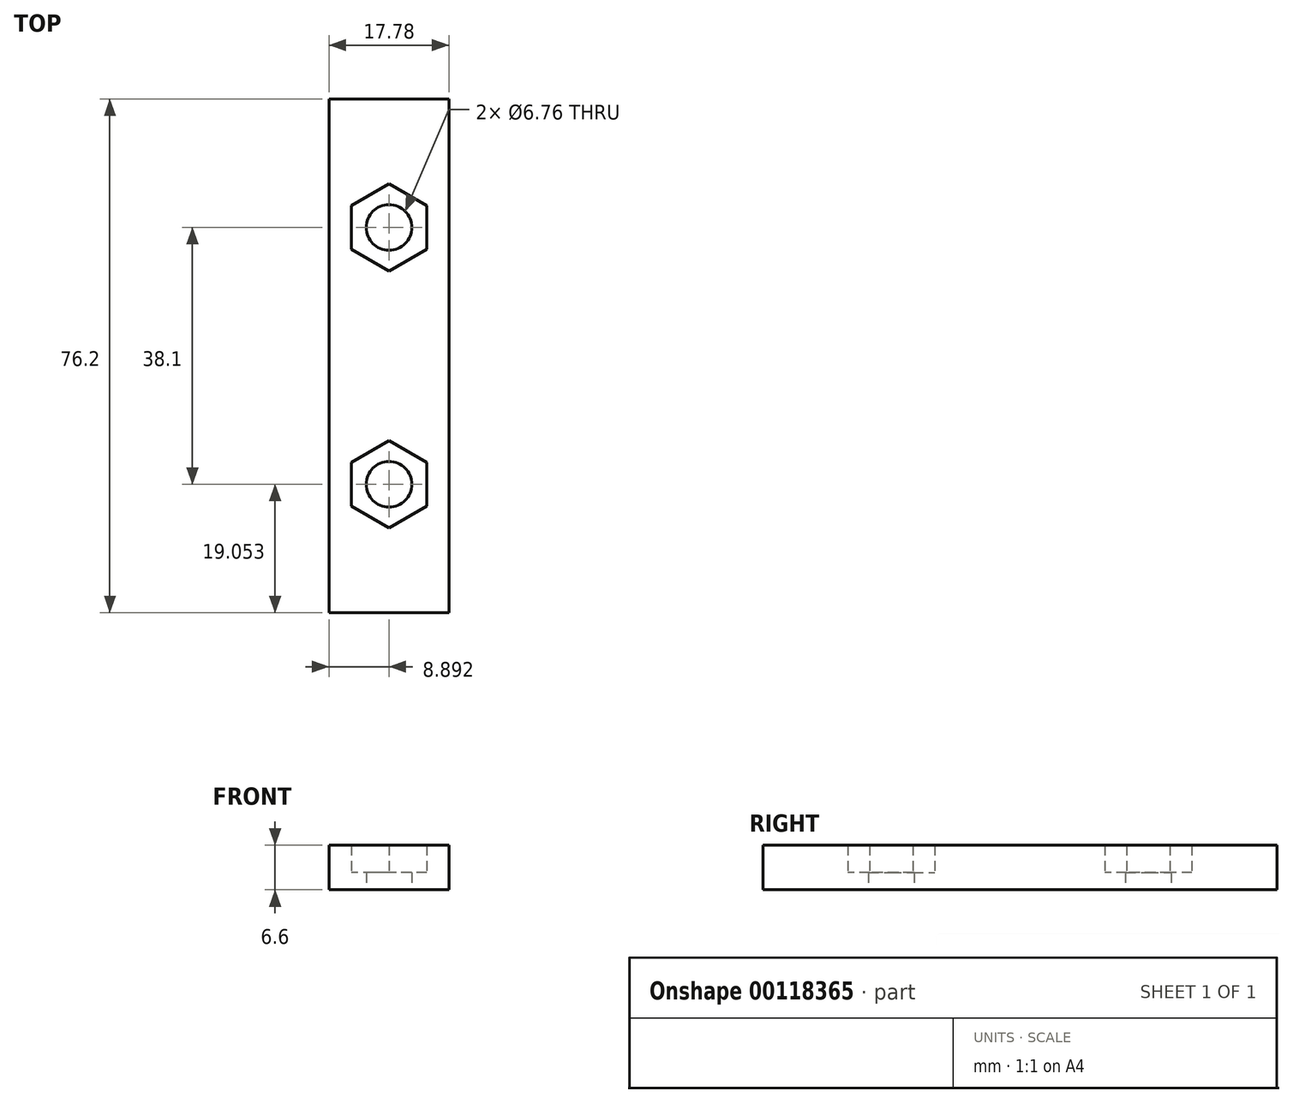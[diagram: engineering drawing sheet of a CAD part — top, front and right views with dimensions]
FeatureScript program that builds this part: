
annotation { "Feature Type Name" : "Feature", "Feature Type Description" : "" }
export const myFeature = defineFeature(function(context is Context, id is Id, definition is map)
    precondition{}
    {
        {
            var Q0;
            Q0=qCreatedBy(makeId("Top.planeOp"),FACE);
            var sketch = newSketch(context, id + "F0", { "sketchPlane" : qUnion([Q0])});
            skLineSegment(sketch, "E0.bottom", {"start": v(-5.89, 167.12) * mm, "end": v(11.9, 167.12) * mm});
            skLineSegment(sketch, "E0.top", {"start": v(-5.89, 90.92) * mm, "end": v(11.9, 90.92) * mm});
            skLineSegment(sketch, "E0.left", {"start": v(-5.89, 167.12) * mm, "end": v(-5.89, 90.92) * mm});
            skLineSegment(sketch, "E0.right", {"start": v(11.9, 167.12) * mm, "end": v(11.9, 90.92) * mm});
            skCircle(sketch, "E1.cCircle", {"center": v(3, 148.07) * mm, "radius": 5.59 * mm, "construction": true});
            skPoint(sketch, "E1.cCircle.centerSnap0", {"position": v(3, 167.12) * mm});
            skLineSegment(sketch, "E1.0", {"start": v(8.59, 151.3) * mm, "end": v(8.59, 144.85) * mm});
            skLineSegment(sketch, "E1.1", {"start": v(8.59, 144.85) * mm, "end": v(3, 141.62) * mm});
            skLineSegment(sketch, "E1.2", {"start": v(3, 141.62) * mm, "end": v(-2.59, 144.85) * mm});
            skLineSegment(sketch, "E1.3", {"start": v(-2.59, 144.85) * mm, "end": v(-2.59, 151.3) * mm});
            skLineSegment(sketch, "E1.4", {"start": v(-2.59, 151.3) * mm, "end": v(3, 154.53) * mm});
            skLineSegment(sketch, "E1.5", {"start": v(3, 154.53) * mm, "end": v(8.59, 151.3) * mm});
            skPoint(sketch, "E1.0.midPoint", {"position": v(8.59, 148.07) * mm});
            skCircle(sketch, "E2.cCircle", {"center": v(3, 109.97) * mm, "radius": 5.59 * mm, "construction": true});
            skLineSegment(sketch, "E2.0", {"start": v(8.59, 106.75) * mm, "end": v(3, 103.52) * mm});
            skLineSegment(sketch, "E2.1", {"start": v(3, 103.52) * mm, "end": v(-2.59, 106.75) * mm});
            skLineSegment(sketch, "E2.2", {"start": v(-2.59, 106.75) * mm, "end": v(-2.59, 113.2) * mm});
            skLineSegment(sketch, "E2.3", {"start": v(-2.59, 113.2) * mm, "end": v(3, 116.43) * mm});
            skLineSegment(sketch, "E2.4", {"start": v(3, 116.43) * mm, "end": v(8.59, 113.2) * mm});
            skLineSegment(sketch, "E2.5", {"start": v(8.59, 113.2) * mm, "end": v(8.59, 106.75) * mm});
            skPoint(sketch, "E2.0.midPoint", {"position": v(5.8, 105.13) * mm});
            skCircle(sketch, "E3", {"center": v(3, 148.07) * mm, "radius": 3.38 * mm});
            skCircle(sketch, "E4", {"center": v(3, 109.97) * mm, "radius": 3.38 * mm});
            skSolve(sketch);
        }
        {
            var Q0;
            Q0=makeQuery(id+"F0.imprint","IMPRINT",FACE,{"disambiguationData":[TD([[makeQuery(id+"F0.imprint","IMPRINT",EDGE,{"derivedFrom":sQuery(id+"F0.wireOp",EDGE,"E0.bottom")}),-1.0]])]});
            extrude(context, id + "F1", {"entities" : qUnion([Q0]), "depth" : 6.6 * mm});
        }
        {
            var Q0;
            Q0=makeQuery(id+"F0.imprint","IMPRINT",FACE,{"disambiguationData":[TD([[makeQuery(id+"F0.imprint","IMPRINT",EDGE,{"derivedFrom":sQuery(id+"F0.wireOp",EDGE,"E2.0")}),-1.0]])]});
            var Q1;
            Q1=makeQuery(id+"F0.imprint","IMPRINT",FACE,{"disambiguationData":[TD([[makeQuery(id+"F0.imprint","IMPRINT",EDGE,{"derivedFrom":sQuery(id+"F0.wireOp",EDGE,"E1.0")}),-1.0]])]});
            extrude(context, id + "F2", {"entities" : qUnion([Q0, Q1]), "operationType" : NewBodyOperationType.ADD, "depth" : 2.54 * mm});
        }
    });
